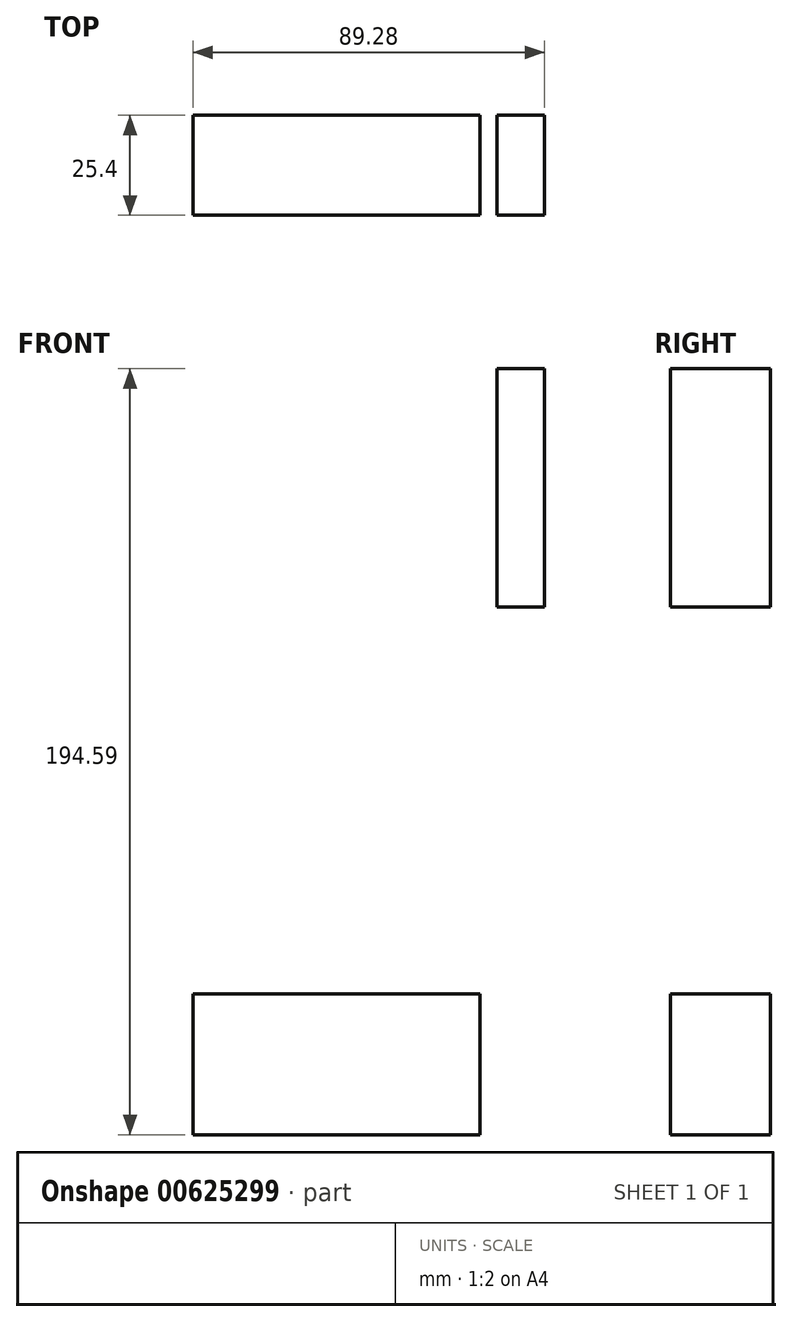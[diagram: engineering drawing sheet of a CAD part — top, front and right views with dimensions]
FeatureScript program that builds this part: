
annotation { "Feature Type Name" : "Feature", "Feature Type Description" : "" }
export const myFeature = defineFeature(function(context is Context, id is Id, definition is map)
    precondition{}
    {
        {
            var Q0;
            Q0=qCreatedBy(makeId("Front.planeOp"),FACE);
            var sketch = newSketch(context, id + "F0", { "sketchPlane" : qUnion([Q0])});
            skLineSegment(sketch, "E0.bottom", {"start": v(-43.69, 35.83) * mm, "end": v(29.2, 35.83) * mm});
            skLineSegment(sketch, "E0.top", {"start": v(-43.69, 0) * mm, "end": v(29.2, 0) * mm});
            skLineSegment(sketch, "E0.left", {"start": v(-43.69, 35.83) * mm, "end": v(-43.69, 0) * mm});
            skLineSegment(sketch, "E0.right", {"start": v(29.2, 35.83) * mm, "end": v(29.2, 0) * mm});
            skLineSegment(sketch, "E1.bottom", {"start": v(33.57, 194.59) * mm, "end": v(45.59, 194.59) * mm});
            skLineSegment(sketch, "E1.top", {"start": v(33.57, 134.08) * mm, "end": v(45.59, 134.08) * mm});
            skLineSegment(sketch, "E1.left", {"start": v(33.57, 194.59) * mm, "end": v(33.57, 134.08) * mm});
            skLineSegment(sketch, "E1.right", {"start": v(45.59, 194.59) * mm, "end": v(45.59, 134.08) * mm});
            skSolve(sketch);
        }
        {
            var Q0;
            Q0 = qSketchRegion(id + "F0", true);
            extrude(context, id + "F1", {"entities" : qUnion([Q0]), "depth" : 25.4 * mm, "offsetDistance" : 25.4 * mm});
        }
    });
